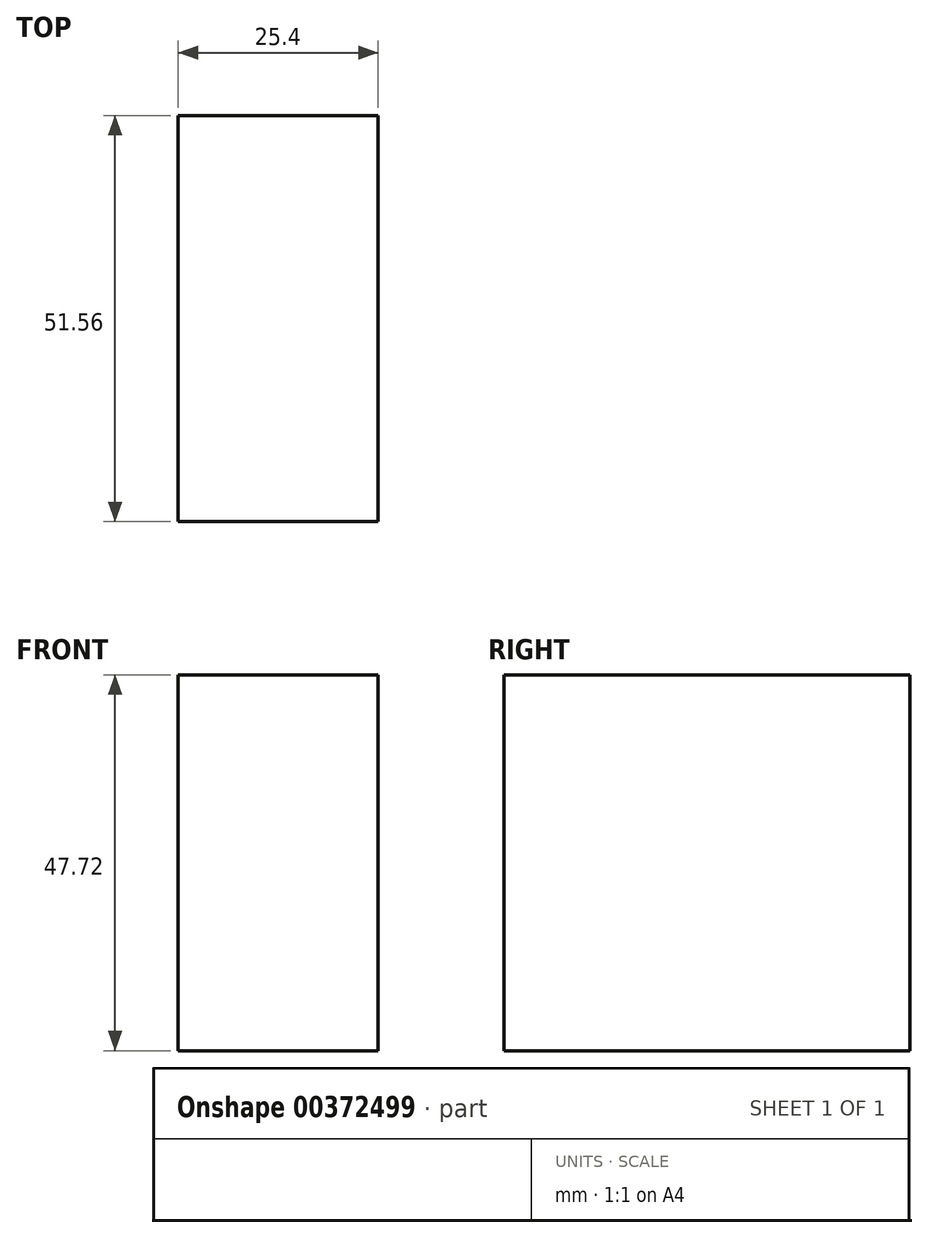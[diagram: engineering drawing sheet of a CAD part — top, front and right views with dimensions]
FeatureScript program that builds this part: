
annotation { "Feature Type Name" : "Feature", "Feature Type Description" : "" }
export const myFeature = defineFeature(function(context is Context, id is Id, definition is map)
    precondition{}
    {
        {
            var Q0;
            Q0=qCreatedBy(makeId("Right.planeOp"),FACE);
            var sketch = newSketch(context, id + "F0", { "sketchPlane" : qUnion([Q0])});
            skLineSegment(sketch, "E0.bottom", {"start": v(0, 0) * mm, "end": v(-51.56, 0) * mm});
            skLineSegment(sketch, "E0.top", {"start": v(0, 47.72) * mm, "end": v(-51.56, 47.72) * mm});
            skLineSegment(sketch, "E0.left", {"start": v(0, 0) * mm, "end": v(0, 47.72) * mm});
            skLineSegment(sketch, "E0.right", {"start": v(-51.56, 0) * mm, "end": v(-51.56, 47.72) * mm});
            skSolve(sketch);
        }
        {
            var Q0;
            Q0 = qSketchRegion(id + "F0", true);
            var Q1;
            Q1=makeQuery(id+"F0.imprint","IMPRINT",FACE,{"disambiguationData":[TD([[makeQuery(id+"F0.imprint","IMPRINT",EDGE,{"derivedFrom":sQuery(id+"F0.wireOp",EDGE,"E0.bottom")}),-1.0]])]});
            extrude(context, id + "F1", {"entities" : qUnion([Q0, Q1]), "depth" : 25.4 * mm});
        }
        {
            var Q0;
            Q0=makeQuery(id+"F1.opExtrude","CAP_FACE",FACE,{"disambiguationData":[OSD([sQuery(id+"F0.wireOp",EDGE,"E0.bottom"),sQuery(id+"F0.wireOp",EDGE,"E0.top"),sQuery(id+"F0.wireOp",EDGE,"E0.left"),sQuery(id+"F0.wireOp",EDGE,"E0.right")])],"isStart":false});
            var sketch = newSketch(context, id + "F2", { "sketchPlane" : qUnion([Q0])});
            skCircle(sketch, "E1", {"center": v(-22.98, 24.12) * mm, "radius": 8.43 * mm});
            skSolve(sketch);
        }
        {
            var Q0;
            Q0 = qSketchRegion(id + "F2", true);
            extrude(context, id + "F3", {"entities" : qUnion([Q0]), "operationType" : NewBodyOperationType.ADD, "depth" : -25.4 * mm});
        }
        {
            var Q0;
            Q0=makeQuery(id+"F1.opExtrude","CAP_FACE",FACE,{"disambiguationData":[OSD([sQuery(id+"F0.wireOp",EDGE,"E0.bottom"),sQuery(id+"F0.wireOp",EDGE,"E0.top"),sQuery(id+"F0.wireOp",EDGE,"E0.left"),sQuery(id+"F0.wireOp",EDGE,"E0.right")])],"isStart":false});
            var sketch = newSketch(context, id + "F4", { "sketchPlane" : qUnion([Q0])});
            skCircle(sketch, "E2", {"center": v(-25.68, 25.23) * mm, "radius": 6.44 * mm});
            skSolve(sketch);
        }
        {
            var Q0;
            Q0 = qSketchRegion(id + "F4", true);
            extrude(context, id + "F5", {"entities" : qUnion([Q0]), "operationType" : NewBodyOperationType.REMOVE, "oppositeDirection" : true, "depth" : -25.4 * mm});
        }
    });
